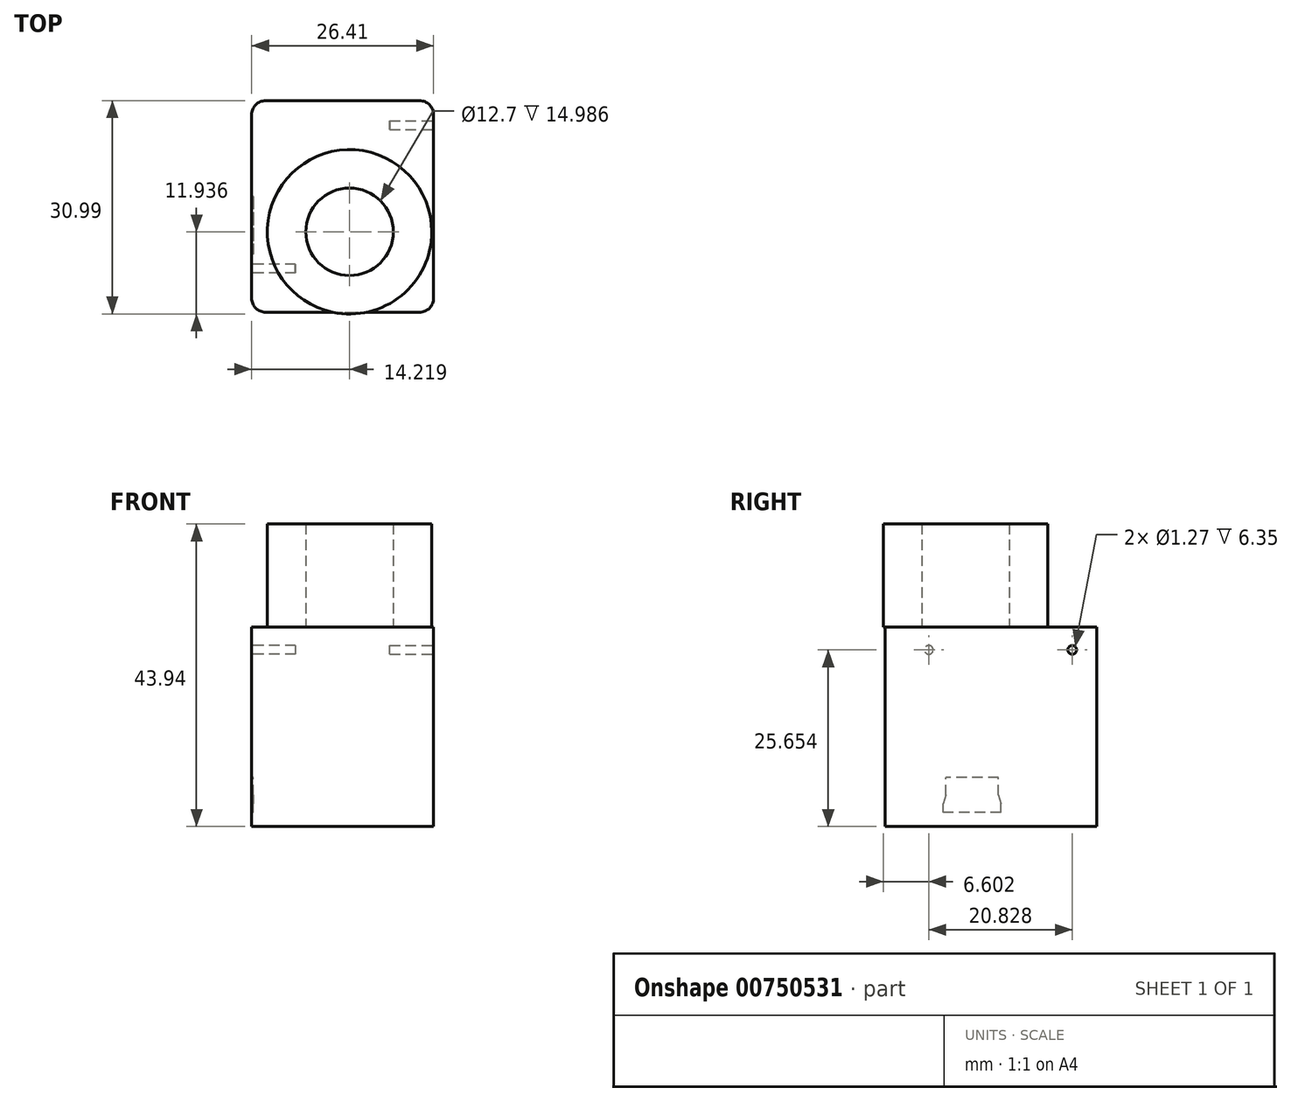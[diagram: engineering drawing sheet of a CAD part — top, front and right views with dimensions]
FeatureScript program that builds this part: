
annotation { "Feature Type Name" : "Feature", "Feature Type Description" : "" }
export const myFeature = defineFeature(function(context is Context, id is Id, definition is map)
    precondition{}
    {
        {
            var Q0;
            Q0=qCreatedBy(makeId("Top.planeOp"),FACE);
            var sketch = newSketch(context, id + "F0", { "sketchPlane" : qUnion([Q0])});
            skCircle(sketch, "E0", {"center": v(0, 0) * mm, "radius": 11.94 * mm});
            skSolve(sketch);
        }
        {
            var Q0;
            Q0 = qSketchRegion(id + "F0", true);
            extrude(context, id + "F1", {"entities" : qUnion([Q0]), "depth" : 15 * mm, "offsetDistance" : 25.4 * mm});
        }
        {
            var Q0;
            Q0=makeQuery(id+"F1.opExtrude","CAP_FACE",FACE,{"disambiguationData":[OSD([sQuery(id+"F0.wireOp",EDGE,"E0")])],"isStart":false});
            var sketch = newSketch(context, id + "F2", { "sketchPlane" : qUnion([Q0])});
            skCircle(sketch, "E1", {"center": v(0, 0) * mm, "radius": 5.28 * mm});
            skSolve(sketch);
        }
        {
            var Q0;
            Q0 = qSketchRegion(id + "F2", true);
            extrude(context, id + "F3", {"entities" : qUnion([Q0]), "operationType" : NewBodyOperationType.REMOVE, "oppositeDirection" : true, "depth" : 6.35 * mm, "offsetDistance" : 25.4 * mm});
        }
        {
            var Q0;
            Q0=qCreatedBy(makeId("Top.planeOp"),FACE);
            var sketch = newSketch(context, id + "F4", { "sketchPlane" : qUnion([Q0])});
            skLineSegment(sketch, "E2.bottom", {"start": v(41.24, 31.67) * mm, "end": v(67.65, 31.67) * mm});
            skLineSegment(sketch, "E2.top", {"start": v(41.24, 0.93) * mm, "end": v(67.65, 0.93) * mm});
            skLineSegment(sketch, "E2.left", {"start": v(41.24, 31.67) * mm, "end": v(41.24, 0.93) * mm});
            skLineSegment(sketch, "E2.right", {"start": v(67.65, 31.67) * mm, "end": v(67.65, 0.93) * mm});
            skSolve(sketch);
        }
        {
            var Q0;
            Q0 = qSketchRegion(id + "F4", true);
            extrude(context, id + "F5", {"entities" : qUnion([Q0]), "depth" : 28.96 * mm, "offsetDistance" : 25.4 * mm});
        }
        {
            var Q0;
            Q0=makeQuery(id+"F5.opExtrude","SWEPT_FACE",FACE,{"disambiguationData":[OSD([sQuery(id+"F4.wireOp",EDGE,"E2.left")])]});
            var sketch = newSketch(context, id + "F6", { "sketchPlane" : qUnion([Q0])});
            skCircle(sketch, "E3", {"center": v(-7.28, 25.65) * mm, "radius": 0.64 * mm});
            skSolve(sketch);
        }
        {
            var Q0;
            Q0 = qSketchRegion(id + "F6", true);
            extrude(context, id + "F7", {"entities" : qUnion([Q0]), "operationType" : NewBodyOperationType.REMOVE, "oppositeDirection" : true, "depth" : 6.35 * mm, "offsetDistance" : 25.4 * mm});
        }
        {
            var Q0;
            Q0=makeQuery(id+"F5.opExtrude","SWEPT_FACE",FACE,{"disambiguationData":[OSD([sQuery(id+"F4.wireOp",EDGE,"E2.right")])]});
            var sketch = newSketch(context, id + "F8", { "sketchPlane" : qUnion([Q0])});
            skCircle(sketch, "E4", {"center": v(28.11, 25.65) * mm, "radius": 0.64 * mm});
            skSolve(sketch);
        }
        {
            var Q0;
            Q0 = qSketchRegion(id + "F8", true);
            extrude(context, id + "F9", {"entities" : qUnion([Q0]), "operationType" : NewBodyOperationType.REMOVE, "oppositeDirection" : true, "depth" : 6.35 * mm, "offsetDistance" : 25.4 * mm});
        }
        {
            var Q0;
            Q0=makeQuery(id+"F5.opExtrude","CAP_FACE",FACE,{"disambiguationData":[OSD([sQuery(id+"F4.wireOp",EDGE,"E2.bottom"),sQuery(id+"F4.wireOp",EDGE,"E2.top"),sQuery(id+"F4.wireOp",EDGE,"E2.left"),sQuery(id+"F4.wireOp",EDGE,"E2.right")])],"isStart":false});
            var sketch = newSketch(context, id + "F10", { "sketchPlane" : qUnion([Q0])});
            skCircle(sketch, "E5", {"center": v(55.46, 12.62) * mm, "radius": 11.94 * mm});
            skCircle(sketch, "E6", {"center": v(55.46, 12.62) * mm, "radius": 6.35 * mm});
            skSolve(sketch);
        }
        {
            var Q0;
            Q0=makeQuery(id+"F10.imprint","IMPRINT",FACE,{"disambiguationData":[TD([[makeQuery(id+"F10.imprint","IMPRINT",EDGE,{"derivedFrom":sQuery(id+"F10.wireOp",EDGE,"E6")}),-1.0]])]});
            var Q1;
            {var subQ0=sQuery(id+"F10.wireOp",EDGE,"E5");var subQ1=makeQuery(id+"F5.opExtrude","CAP_EDGE",EDGE,{"disambiguationData":[OSD([sQuery(id+"F4.wireOp",EDGE,"E2.top")])],"isStart":false});var subQ2=makeQuery(id+"F10.imprint","INTERSECT",VERTEX,{"disambiguationData":[OD(0.0)],"derivedFrom":[subQ1,subQ0]});Q1=makeQuery(id+"F10.imprint","IMPRINT",FACE,{"disambiguationData":[TD([[makeQuery(id+"F10.imprint","IMPRINT",EDGE,{"disambiguationData":[TD([[subQ2,-1.0]])],"derivedFrom":subQ0}),1.0]])]});}
            extrude(context, id + "F11", {"entities" : qUnion([Q0, Q1]), "operationType" : NewBodyOperationType.ADD, "depth" : 15 * mm, "offsetDistance" : 25.4 * mm});
        }
        {
            var Q0;
            Q0=makeQuery(id+"F1.opExtrude","SWEPT_BODY",BODY,{"disambiguationData":[OSD([sQuery(id+"F0.wireOp",EDGE,"E0")])]});
            deleteBodies(context, id + "F12", {"entities" : qUnion([Q0])});
        }
        {
            var Q0;
            Q0=makeQuery(id+"F5.opExtrude","SWEPT_EDGE",EDGE,{"disambiguationData":[OSD([sQuery(id+"F4.wireOp",EDGE,"E2.bottom"),sQuery(id+"F4.wireOp",EDGE,"E2.left")])]});
            var Q1;
            Q1=makeQuery(id+"F5.opExtrude","SWEPT_EDGE",EDGE,{"disambiguationData":[OSD([sQuery(id+"F4.wireOp",EDGE,"E2.bottom"),sQuery(id+"F4.wireOp",EDGE,"E2.right")])]});
            var Q2;
            Q2=makeQuery(id+"F5.opExtrude","SWEPT_EDGE",EDGE,{"disambiguationData":[OSD([sQuery(id+"F4.wireOp",EDGE,"E2.top"),sQuery(id+"F4.wireOp",EDGE,"E2.left")])]});
            var Q3;
            Q3=makeQuery(id+"F5.opExtrude","SWEPT_EDGE",EDGE,{"disambiguationData":[OSD([sQuery(id+"F4.wireOp",EDGE,"E2.top"),sQuery(id+"F4.wireOp",EDGE,"E2.right")])]});
            fillet(context, id + "F13", {"entities" : qUnion([Q0, Q1, Q2, Q3]), "radius" : 2.03 * mm, "tangentPropagation" : true, "allowEdgeOverflow" : false});
        }
        {
            var Q0;
            Q0=makeQuery(id+"F5.opExtrude","SWEPT_FACE",FACE,{"disambiguationData":[OSD([sQuery(id+"F4.wireOp",EDGE,"E2.left")])]});
            var sketch = newSketch(context, id + "F14", { "sketchPlane" : qUnion([Q0])});
            skLineSegment(sketch, "E7.bottom", {"start": v(-17.39, 2.03) * mm, "end": v(-9.77, 2.03) * mm});
            skLineSegment(sketch, "E7.top", {"start": v(-17.39, 7.11) * mm, "end": v(-9.77, 7.11) * mm});
            skLineSegment(sketch, "E7.left", {"start": v(-17.39, 2.03) * mm, "end": v(-17.39, 7.11) * mm});
            skLineSegment(sketch, "E7.right", {"start": v(-9.77, 2.03) * mm, "end": v(-9.77, 7.11) * mm});
            skLineSegment(sketch, "E8.bottom", {"start": v(-17.39, 2.03) * mm, "end": v(-17.77, 2.03) * mm});
            skLineSegment(sketch, "E8.top", {"start": v(-17.39, 3.3) * mm, "end": v(-17.77, 3.3) * mm});
            skLineSegment(sketch, "E8.left", {"start": v(-17.39, 2.03) * mm, "end": v(-17.39, 3.3) * mm});
            skLineSegment(sketch, "E8.right", {"start": v(-17.77, 2.03) * mm, "end": v(-17.77, 3.3) * mm});
            skLineSegment(sketch, "E9.bottom", {"start": v(-9.77, 2.03) * mm, "end": v(-9.39, 2.03) * mm});
            skLineSegment(sketch, "E9.top", {"start": v(-9.77, 3.3) * mm, "end": v(-9.39, 3.3) * mm});
            skLineSegment(sketch, "E9.left", {"start": v(-9.77, 2.03) * mm, "end": v(-9.77, 3.3) * mm});
            skLineSegment(sketch, "E9.right", {"start": v(-9.39, 2.03) * mm, "end": v(-9.39, 3.3) * mm});
            skLineSegment(sketch, "E10", {"start": v(-17.39, 4.57) * mm, "end": v(-17.77, 3.3) * mm});
            skLineSegment(sketch, "E11", {"start": v(-9.77, 4.57) * mm, "end": v(-9.39, 3.3) * mm});
            skSolve(sketch);
        }
        {
            var Q0;
            Q0=makeQuery(id+"F14.imprint","IMPRINT",FACE,{"disambiguationData":[TD([[makeQuery(id+"F14.imprint","IMPRINT",EDGE,{"derivedFrom":sQuery(id+"F14.wireOp",EDGE,"E7.bottom")}),1.0]])]});
            var Q1;
            Q1=makeQuery(id+"F14.imprint","IMPRINT",FACE,{"disambiguationData":[TD([[makeQuery(id+"F14.imprint","IMPRINT",EDGE,{"derivedFrom":sQuery(id+"F14.wireOp",EDGE,"E8.bottom")}),-1.0]])]});
            var Q2;
            {var subQ0=sQuery(id+"F14.wireOp",EDGE,"E8.top");Q2=makeQuery(id+"F14.imprint","IMPRINT",FACE,{"disambiguationData":[TD([[makeQuery(id+"F14.imprint","IMPRINT",EDGE,{"derivedFrom":subQ0}),-1.0]])]});}
            var Q3;
            {var subQ0=sQuery(id+"F14.wireOp",EDGE,"E9.top");Q3=makeQuery(id+"F14.imprint","IMPRINT",FACE,{"disambiguationData":[TD([[makeQuery(id+"F14.imprint","IMPRINT",EDGE,{"derivedFrom":subQ0}),1.0]])]});}
            var Q4;
            Q4=makeQuery(id+"F14.imprint","IMPRINT",FACE,{"disambiguationData":[TD([[makeQuery(id+"F14.imprint","IMPRINT",EDGE,{"derivedFrom":sQuery(id+"F14.wireOp",EDGE,"E9.bottom")}),1.0]])]});
            extrude(context, id + "F15", {"entities" : qUnion([Q0, Q1, Q2, Q3, Q4]), "operationType" : NewBodyOperationType.REMOVE, "oppositeDirection" : true, "depth" : 0.25 * mm, "offsetDistance" : 25.4 * mm});
        }
    });
